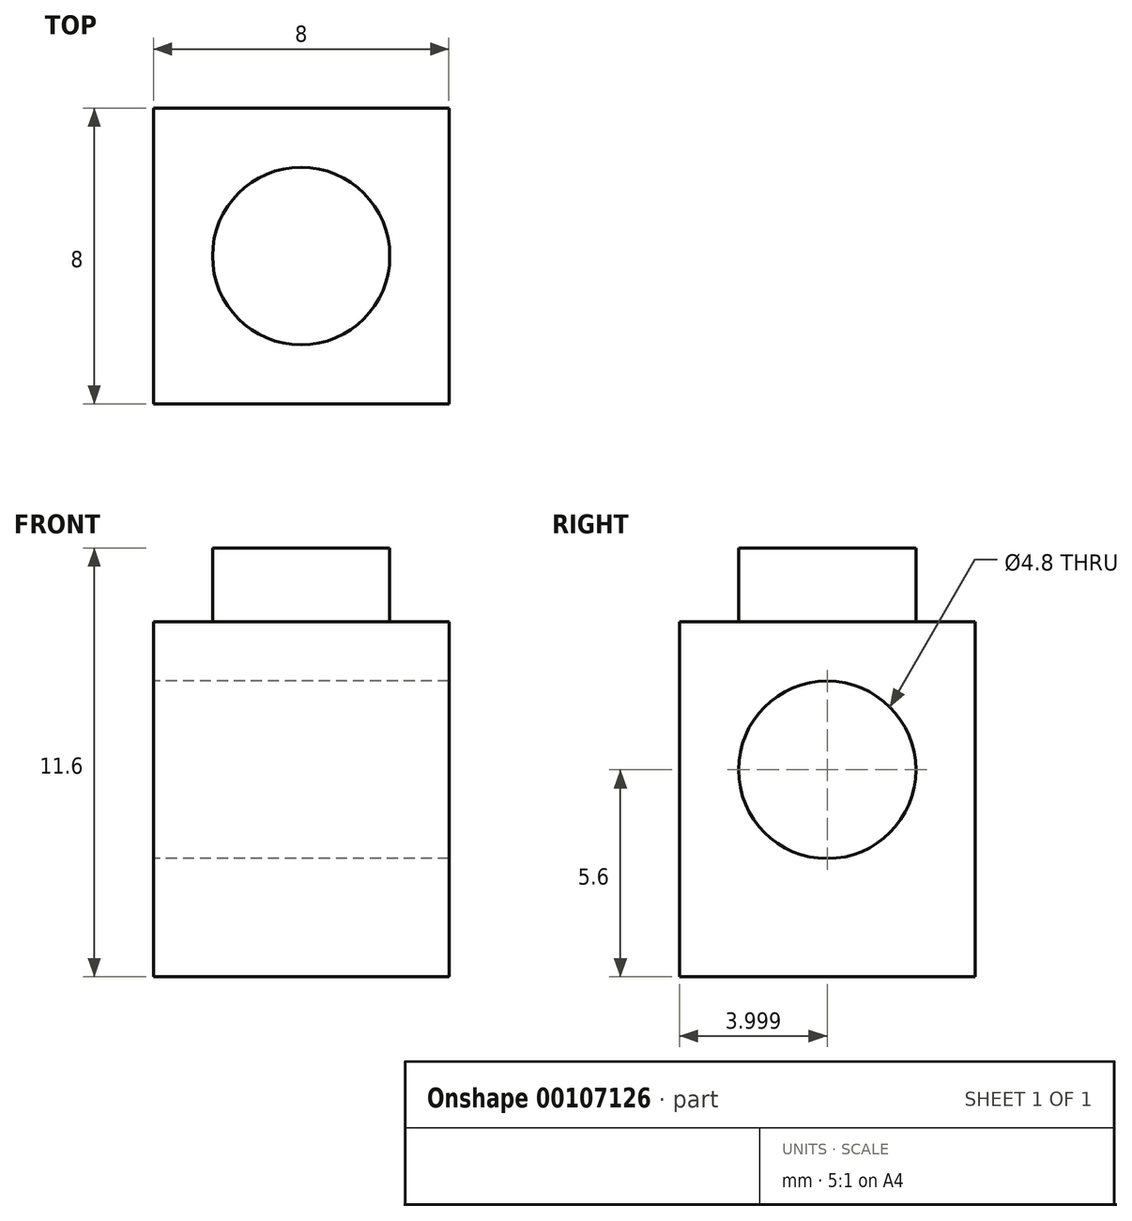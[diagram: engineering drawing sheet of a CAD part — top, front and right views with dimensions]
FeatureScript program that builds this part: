
annotation { "Feature Type Name" : "Feature", "Feature Type Description" : "" }
export const myFeature = defineFeature(function(context is Context, id is Id, definition is map)
    precondition{}
    {
        {
            var Q0;
            Q0=qCreatedBy(makeId("Top.planeOp"),FACE);
            var sketch = newSketch(context, id + "F0", { "sketchPlane" : qUnion([Q0])});
            skLineSegment(sketch, "E0.0", {"start": v(3.6, 4.4) * mm, "end": v(3.6, -3.6) * mm});
            skLineSegment(sketch, "E0.1", {"start": v(3.6, -3.6) * mm, "end": v(-4.4, -3.6) * mm});
            skLineSegment(sketch, "E0.2", {"start": v(-4.4, -3.6) * mm, "end": v(-4.4, 4.4) * mm});
            skLineSegment(sketch, "E0.3", {"start": v(-4.4, 4.4) * mm, "end": v(3.6, 4.4) * mm});
            skPoint(sketch, "E0.0.midPoint", {"position": v(3.6, 0.4) * mm});
            skSolve(sketch);
        }
        {
            var Q0;
            Q0=makeQuery(id+"F0.imprint","IMPRINT",FACE,{"disambiguationData":[TD([[makeQuery(id+"F0.imprint","IMPRINT",EDGE,{"derivedFrom":sQuery(id+"F0.wireOp",EDGE,"E0.0")}),-1.0]])]});
            extrude(context, id + "F1", {"entities" : qUnion([Q0]), "depth" : 9.6 * mm});
        }
        {
            var Q0;
            Q0=makeQuery(id+"F1.opExtrude","SWEPT_FACE",FACE,{"disambiguationData":[OSD([sQuery(id+"F0.wireOp",EDGE,"E0.2")])]});
            var sketch = newSketch(context, id + "F2", { "sketchPlane" : qUnion([Q0])});
            skLineSegment(sketch, "E1", {"start": v(-0.4, 0) * mm, "end": v(-0.4, 5.6) * mm});
            skCircle(sketch, "E2", {"center": v(-0.4, 5.6) * mm, "radius": 2.4 * mm});
            skSolve(sketch);
        }
        {
            var Q0;
            Q0=makeQuery(id+"F2.imprint","IMPRINT",FACE,{"disambiguationData":[TD([[makeQuery(id+"F2.imprint","IMPRINT",EDGE,{"derivedFrom":sQuery(id+"F2.wireOp",EDGE,"E2")}),1.0]])]});
            extrude(context, id + "F3", {"entities" : qUnion([Q0]), "operationType" : NewBodyOperationType.REMOVE, "oppositeDirection" : true, "depth" : 25 * mm});
        }
        {
            var Q0;
            Q0=makeQuery(id+"F1.opExtrude","CAP_FACE",FACE,{"disambiguationData":[OSD([sQuery(id+"F0.wireOp",EDGE,"E0.0"),sQuery(id+"F0.wireOp",EDGE,"E0.1"),sQuery(id+"F0.wireOp",EDGE,"E0.2"),sQuery(id+"F0.wireOp",EDGE,"E0.3")])],"isStart":false});
            var sketch = newSketch(context, id + "F4", { "sketchPlane" : qUnion([Q0])});
            skLineSegment(sketch, "E3", {"start": v(-0.4, -3.6) * mm, "end": v(-0.4, 0.4) * mm, "construction": true});
            skCircle(sketch, "E4", {"center": v(-0.4, 0.4) * mm, "radius": 2.4 * mm});
            skSolve(sketch);
        }
        {
            var Q0;
            Q0=makeQuery(id+"F4.imprint","IMPRINT",FACE,{"disambiguationData":[TD([[makeQuery(id+"F4.imprint","IMPRINT",EDGE,{"derivedFrom":sQuery(id+"F4.wireOp",EDGE,"E4")}),1.0]])]});
            extrude(context, id + "F5", {"entities" : qUnion([Q0]), "operationType" : NewBodyOperationType.ADD, "depth" : 2 * mm});
        }
    });
